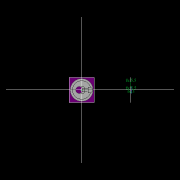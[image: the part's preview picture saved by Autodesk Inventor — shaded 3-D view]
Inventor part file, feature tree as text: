
AUTODESK INVENTOR PART (.ipt)
format: ipt  version: 2022.2 (Build 262287010, 287A)  size: 541,696 bytes
history: native  units: mm
features: other x20, extrude x19, sketch x13, pattern_circular x7, plane x5, fillet x2, move_body x2, revolve x2, draft x2, chamfer x2, loft x1
ambient origin geometry x8: Origin, YZ Plane, XZ Plane, XY Plane, X Axis, Y Axis, Z Axis, Center Point
bodies: Solid5 (feature_tree)
feature tree (75):
  other  "CrossSection1"
  sketch  "Sketch7"  dims[d90=15.767323mm]
  other  "Roller1"
  other  "Roller2"
  sketch  "Sketch22"  dims[d167=8.972256mm]
  sketch  "Sketch2"  dims[d57=4.025mm]
  sketch  "Sketch23"  dims[d173=10.814812mm]
  other  "RevRoller1"
  fillet  "Fillet1"  Radius=13.336791mm
  pattern_circular  "Circular Pattern13"  Count=360  [1 undecoded]
  move_body  "Move Body7"
  revolve  "Revolution13"  [1 undecoded]
  fillet  "Fillet3"  Radius=0.025mm
  pattern_circular  "Circular Pattern14"  [2 undecoded]
  move_body  "Move Body6"
  revolve  "Revolution14"  [1 undecoded]
  plane  "Work Plane7"
  sketch  "Sketch44"  dims[d349=17.374602mm]
  plane  "Work Plane8"
  loft  "Loft1"
  sketch  "Sketch46"  dims[d351=0.025mm]
  extrude  "Extrusion39"  Depth=5.5mm
  plane  "Work Plane9"
  sketch  "Sketch47"  dims[d352=0.025mm d354=0.025mm d355=17.374329mm d356=17.374602mm d357=1.0mm d358=90.0deg d359=0.5mm d360=60.0mm d361=360.0deg d363=30.0deg d367=8.1mm d369=4.014775mm d370=0.025mm d371=1.0mm d372=30.0deg d373=90.0deg d374=0.5mm d375=60.0mm d376=360.0deg d378=90.0deg d379=0.1mm d380=0.025mm d381=0.025mm d382=0.025mm d383=0.025mm d384=10.461905mm d385=0.0mm d386=0.0mm d391=1.0mm d392=53.5mm d393=1.5mm d394=1.5mm d395=1.5mm d396=1.5mm d397=90.0deg d398=90.0deg d399=90.0deg d400=53.5mm d401=10.461905mm d402=0.0mm d486=0.436332mm d487=0.5mm d488=2.0mm d489=0.0mm d490=20.0mm d495=2.5mm d496=8.0mm d506=13.856406mm d507=55.5mm d508=8.0mm d509=0.05mm d510=2.5mm d511=30.0deg d512=12.0mm d513=6.0mm d514=0.2mm d515=30.0deg d516=131.0mm d517=65.5mm d518=0.2mm d519=100.0mm d520=120.0mm d521=2.0mm d522=150.0mm d530=50.0mm d531=5.5mm d532=5.5mm d533=5.5mm d534=85.75mm d535=73.5mm d536=61.25mm d537=24.5mm d538=3.0mm d539=2.4mm d540=0.0mm d541=0.0mm d542=0.0mm d543=5.5mm d544=3.0mm d545=0.0mm d546=90.0mm d547=360.0deg d549=3.0mm d550=3.0mm d551=2.4mm d552=0.0mm d553=5.230953mm d554=0.0mm d555=2.4mm d556=0.0mm d557=5.230953mm d558=0.0mm d559=5.230953mm d560=0.0mm d561=90.0mm d562=360.0deg d564=60.0mm d565=360.0deg d567=5.5mm d568=5.5mm d569=3.0mm d570=0.0mm d571=5.230953mm d572=0.0mm d573=3.0mm d574=0.0mm d575=5.230953mm d576=0.0mm d577=90.0mm d578=360.0deg d580=60.0mm d581=360.0deg d584=20.0mm d585=8.0mm d587=1.75mm d589=3.0mm d592=2.0mm d593=12.0mm d594=12.0mm d600=0.5mm d601=2.0mm d602=45.0deg d603=0.5mm d604=2.0mm d605=45.0deg d606=0.436332mm d607=0.5mm d608=0.0mm d609=20.0mm d611=360.0deg d613=0.0mm d614=0.0mm d615=20.0mm d616=3.611mm d617=0.0mm d618=90.0deg d619=0.0mm d620=90.0deg d621=2.5mm d622=7.0mm d623=0.0mm d624=0.0mm d625=50.0mm d626=5.5mm d627=3.0mm d628=5.5mm d629=43.459mm d630=0.0mm d631=52.538mm d632=0.0mm d633=4.8mm d634=0.0mm d16=0.872665mm d17=0.872665mm d49=0.872665mm d50=0.872665mm d51=0.872665mm d52=0.872665mm d236=0.5mm d237=0.872665mm d238=0.5mm d239=0.872665mm d282=1.0mm d283=1.0mm d284=1.0mm d285=0.15mm d286=0.25mm d287=0.375mm d288=14.3117mm d289=0.75mm d290=20.594885mm d291=0.0625mm d292=0.75mm d293=0.375mm d405=0.5mm d406=0.872665mm d407=0.5mm d408=0.872665mm d413=0.5mm d414=0.872665mm d415=0.5mm d416=0.872665mm d417=0.5mm d418=0.872665mm d419=0.5mm d420=0.872665mm d421=0.872665mm d431=0.5mm d432=0.872665mm d433=0.5mm d434=0.872665mm d471=0.5mm d472=0.872665mm d473=0.5mm d474=0.872665mm d497=0.5mm d498=0.872665mm d499=0.5mm d500=0.872665mm d590=0.5mm d591=0.872665mm]
  extrude  "Extrusion40"  TaperAngle=90.0deg  [1 undecoded]
  extrude  "Extrusion41"  Depth=5.5mm
  extrude  "Extrusion42"  Depth=5.5mm
  other  "OuterRim_Top2"
  other  "OuterRim_Bottom2"
  extrude  "Rotor_Ring"  TaperAngle=360.0deg  [1 undecoded]
  draft  "FaceDraft2"
  sketch  "Sketch30"  dims[d201=53.5mm d232=0.0mm d233=3600.0mm]
  plane  "Work Plane5"
  other  "Rotor Featurs"
  other  "RotorRim_Bottom"
  extrude  "Extrusion24"  TaperAngle=30.0deg  [1 undecoded]
  extrude  "Extrusion25"  Depth=5.5mm
  extrude  "Extrusion26"  Depth=5.5mm
  pattern_circular  "Circular Pattern23"  [2 undecoded]
  sketch  "Sketch41"  dims[d346=0.025mm]
  extrude  "Extrusion27"  Depth=5.5mm
  extrude  "Extrusion28"  TaperAngle=30.0deg  [1 undecoded]
  pattern_circular  "Circular Pattern24"  Angle=90.0deg  [1 undecoded]
  extrude  "Extrusion29"  Depth=5.5mm
  extrude  "Extrusion30"  Depth=5.5mm
  extrude  "Extrusion31"  TaperAngle=360.0deg  [1 undecoded]
  pattern_circular  "Circular Pattern25"  Angle=90.0deg  [1 undecoded]
  sketch  "Sketch42"  dims[d347=0.1mm]
  extrude  "Extrusion32"  Depth=0.1mm
  extrude  "Extrusion33"  Depth=5.5mm
  extrude  "Extrusion34"  Depth=5.5mm
  extrude  "Extrusion35"  Depth=5.5mm
  pattern_circular  "Circular Pattern26"  [2 undecoded]
  pattern_circular  "Circular Pattern27"  [2 undecoded]
  chamfer  "Chamfer1"  [1 undecoded]
  chamfer  "Chamfer2"  [1 undecoded]
  draft  "FaceDraft4"
  plane  "Work Plane6"
  sketch  "Sketch43"  dims[d348=0.1mm]
  extrude  "Extrusion37"  Depth=5.5mm
  extrude  "Extrusion38"  Depth=5.5mm
  other  "2D Equation Curve1"
  sketch  "Sketch40"  dims[d343=17.374329mm d344=17.374602mm d345=0.025mm]
  other  "Work Axis6"
  other  "Work Axis7"
  other  "Work Axis8"
  other  "Work Axis9"
  other  "Work Axis10"
  other  "Work Point1"
  other  "Work Point2"
  other  "Work Point3"
  other  "Work Point4"
  other  "Work Point5"
  sketch  "Sketch45"  dims[d350=17.374329mm]
  other  "Edges1"
note: 20 required parameter values undecoded (feature->parameter linkage not recoverable at this tier; creation-order binding heuristic only, values carry confidence <= 0.55)